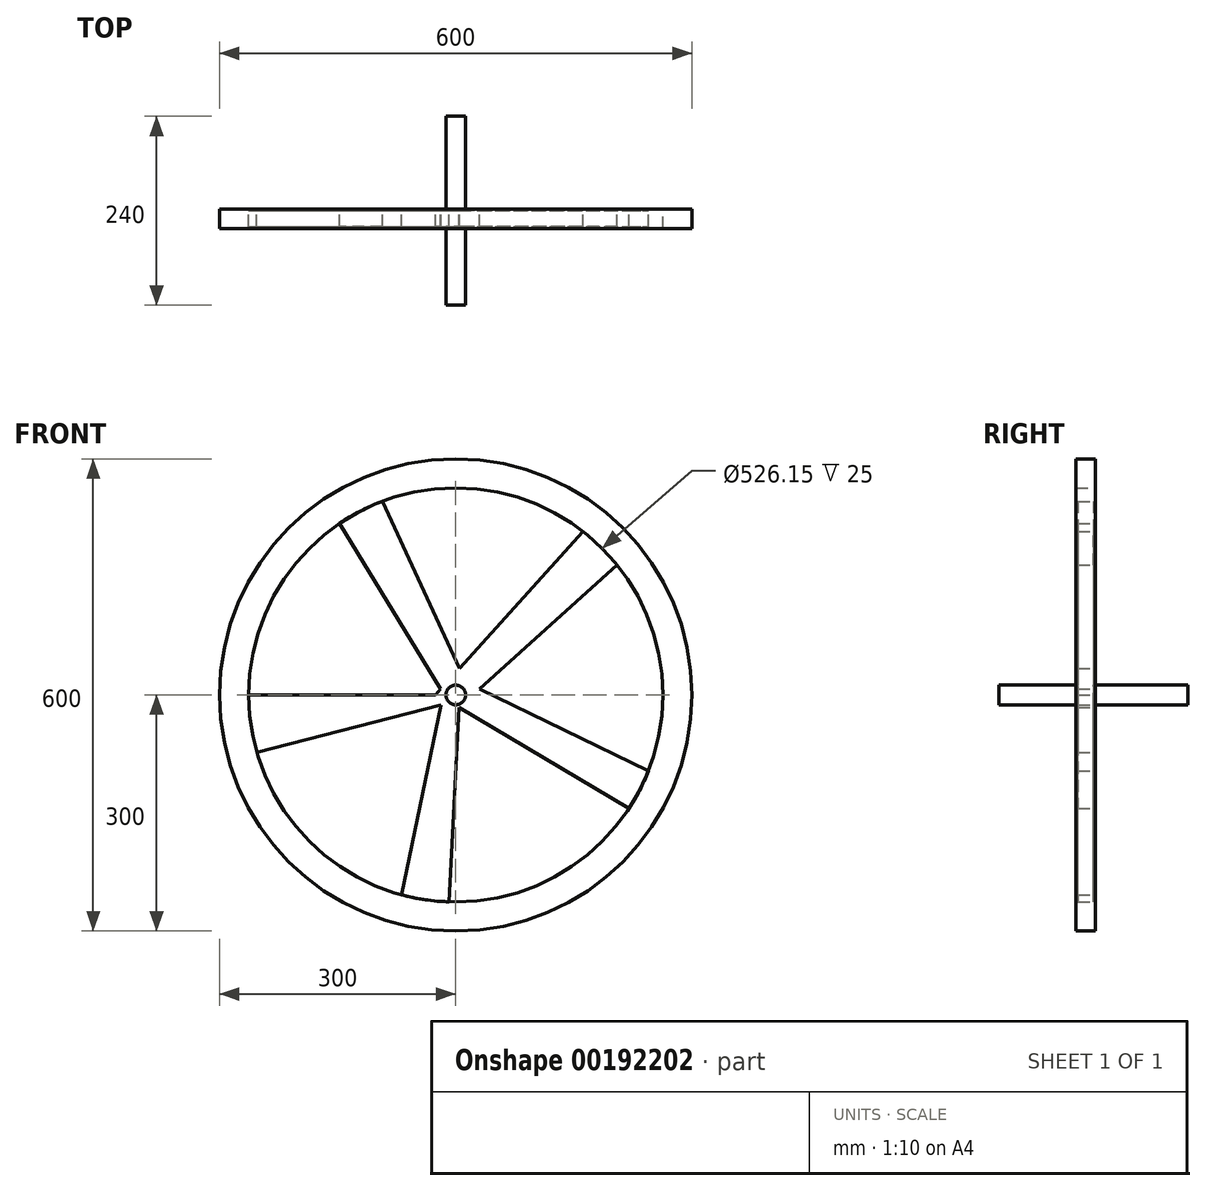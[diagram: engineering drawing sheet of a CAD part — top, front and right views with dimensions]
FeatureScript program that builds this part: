
annotation { "Feature Type Name" : "Feature", "Feature Type Description" : "" }
export const myFeature = defineFeature(function(context is Context, id is Id, definition is map)
    precondition{}
    {
        {
            var Q0;
            Q0=qCreatedBy(makeId("Front.planeOp"),FACE);
            var sketch = newSketch(context, id + "F0", { "sketchPlane" : qUnion([Q0])});
            skCircle(sketch, "E0", {"center": v(0, 0) * mm, "radius": 300 * mm});
            skCircle(sketch, "E1", {"center": v(0, 0) * mm, "radius": 263.08 * mm});
            skLineSegment(sketch, "E2.0", {"start": v(-42.18, -280.34) * mm, "end": v(-69.08, -253.84) * mm});
            skLineSegment(sketch, "E2.2", {"start": v(-130.66, 251.59) * mm, "end": v(-93.32, 245.97) * mm});
            skLineSegment(sketch, "E2.3", {"start": v(198.9, 202) * mm, "end": v(205.1, 164.76) * mm});
            skLineSegment(sketch, "E2.4", {"start": v(253.58, -126.74) * mm, "end": v(220.07, -144.14) * mm});
            skPoint(sketch, "E2.0.midPoint", {"position": v(-160.91, -163.43) * mm});
            skLineSegment(sketch, "E3", {"start": v(-147.54, 217.81) * mm, "end": v(-19.08, 7.43) * mm});
            skLineSegment(sketch, "E4", {"start": v(-93.32, 245.97) * mm, "end": v(12.84, 15.73) * mm});
            skLineSegment(sketch, "E5", {"start": v(12.84, 15.73) * mm, "end": v(244.63, -96.78) * mm});
            skLineSegment(sketch, "E6", {"start": v(-9.72, -7.9) * mm, "end": v(-6.77, -9.64) * mm});
            skLineSegment(sketch, "E7", {"start": v(161.56, 207.63) * mm, "end": v(4.58, 33.65) * mm});
            skLineSegment(sketch, "E8", {"start": v(205.1, 164.76) * mm, "end": v(30.14, 7.33) * mm});
            skLineSegment(sketch, "E9", {"start": v(-263.08, 0) * mm, "end": v(-25.78, 0) * mm});
            skLineSegment(sketch, "E10", {"start": v(-252.74, -73.01) * mm, "end": v(-18.49, -12.66) * mm});
            skLineSegment(sketch, "E11", {"start": v(-8.66, -262.93) * mm, "end": v(4.11, -16.1) * mm});
            skLineSegment(sketch, "E12.trimOffspring", {"start": v(-19.08, 7.43) * mm, "end": v(-25.78, 0) * mm});
            skLineSegment(sketch, "E13", {"start": v(-69.08, -253.84) * mm, "end": v(-18.49, -12.66) * mm});
            skLineSegment(sketch, "E14.trimOffspring", {"start": v(4.11, -16.1) * mm, "end": v(220.07, -144.14) * mm});
            skPoint(sketch, "E15.end.orphan", {"position": v(12.84, 5.87) * mm});
            skPoint(sketch, "E16.trimOffspring.end.orphan", {"position": v(0, -7.9) * mm});
            skLineSegment(sketch, "E17.trimOffspring", {"start": v(-147.54, 217.81) * mm, "end": v(-130.66, 251.59) * mm});
            skPoint(sketch, "E18.orphan", {"position": v(-279.65, -46.52) * mm});
            skLineSegment(sketch, "E19.trimOffspring", {"start": v(247.39, -89.5) * mm, "end": v(253.58, -126.74) * mm});
            skLineSegment(sketch, "E20.trimOffspring", {"start": v(-8.66, -262.93) * mm, "end": v(-42.18, -280.34) * mm});
            skLineSegment(sketch, "E21", {"start": v(161.56, 207.63) * mm, "end": v(198.9, 202) * mm});
            skLineSegment(sketch, "E22", {"start": v(-252.74, -73.01) * mm, "end": v(-279.65, -46.52) * mm});
            skLineSegment(sketch, "E23", {"start": v(-279.65, -46.52) * mm, "end": v(-263.08, 0) * mm});
            skSolve(sketch);
        }
        {
            var Q0;
            Q0=makeQuery(id+"F0.imprint","IMPRINT",FACE,{"disambiguationData":[TD([[makeQuery(id+"F0.imprint","IMPRINT",EDGE,{"derivedFrom":sQuery(id+"F0.wireOp",EDGE,"E0")}),1.0]])]});
            var Q1;
            {var subQ0=sQuery(id+"F0.wireOp",EDGE,"E2.2");Q1=makeQuery(id+"F0.imprint","IMPRINT",FACE,{"disambiguationData":[TD([[makeQuery(id+"F0.imprint","IMPRINT",EDGE,{"derivedFrom":subQ0}),-1.0]])]});}
            var Q2;
            {var subQ2=sQuery(id+"F0.wireOp",EDGE,"E22");Q2=makeQuery(id+"F0.imprint","IMPRINT",FACE,{"disambiguationData":[TD([[makeQuery(id+"F0.imprint","IMPRINT",EDGE,{"derivedFrom":subQ2}),-1.0]])]});}
            var Q3;
            {var subQ0=sQuery(id+"F0.wireOp",EDGE,"E2.0");Q3=makeQuery(id+"F0.imprint","IMPRINT",FACE,{"disambiguationData":[TD([[makeQuery(id+"F0.imprint","IMPRINT",EDGE,{"derivedFrom":subQ0}),-1.0]])]});}
            var Q4;
            {var subQ0=sQuery(id+"F0.wireOp",EDGE,"E2.4");Q4=makeQuery(id+"F0.imprint","IMPRINT",FACE,{"disambiguationData":[TD([[makeQuery(id+"F0.imprint","IMPRINT",EDGE,{"derivedFrom":subQ0}),-1.0]])]});}
            var Q5;
            {var subQ0=sQuery(id+"F0.wireOp",EDGE,"E2.3");Q5=makeQuery(id+"F0.imprint","IMPRINT",FACE,{"disambiguationData":[TD([[makeQuery(id+"F0.imprint","IMPRINT",EDGE,{"derivedFrom":subQ0}),-1.0]])]});}
            extrude(context, id + "F1", {"entities" : qUnion([Q0, Q1, Q2, Q3, Q4, Q5]), "depth" : 25 * mm, "symmetric" : true});
        }
        {
            var Q0;
            {var subQ7=sQuery(id+"F0.wireOp",EDGE,"E3");Q0=makeQuery(id+"F0.imprint","IMPRINT",FACE,{"disambiguationData":[TD([[makeQuery(id+"F0.imprint","IMPRINT",EDGE,{"derivedFrom":subQ7}),1.0]])]});}
            var Q1;
            {var subQ0=sQuery(id+"F0.wireOp",EDGE,"E7");Q1=makeQuery(id+"F0.imprint","IMPRINT",FACE,{"disambiguationData":[TD([[makeQuery(id+"F0.imprint","IMPRINT",EDGE,{"derivedFrom":subQ0}),1.0]])]});}
            extrude(context, id + "F2", {"entities" : qUnion([Q0, Q1]), "operationType" : NewBodyOperationType.ADD, "depth" : 20 * mm, "symmetric" : true});
        }
        {
            var Q0;
            Q0=makeQuery(id+"F2.opExtrude","CAP_FACE",FACE,{"disambiguationData":[OSD([sQuery(id+"F0.wireOp",EDGE,"E1"),sQuery(id+"F0.wireOp",EDGE,"E3"),sQuery(id+"F0.wireOp",EDGE,"E4"),sQuery(id+"F0.wireOp",EDGE,"E5"),sQuery(id+"F0.wireOp",EDGE,"E7"),sQuery(id+"F0.wireOp",EDGE,"E8"),sQuery(id+"F0.wireOp",EDGE,"E9"),sQuery(id+"F0.wireOp",EDGE,"E10"),sQuery(id+"F0.wireOp",EDGE,"E11"),sQuery(id+"F0.wireOp",EDGE,"E12.trimOffspring"),sQuery(id+"F0.wireOp",EDGE,"E13"),sQuery(id+"F0.wireOp",EDGE,"E14.trimOffspring")])],"isStart":true});
            var sketch = newSketch(context, id + "F3", { "sketchPlane" : qUnion([Q0])});
            skCircle(sketch, "E24", {"center": v(0, 0) * mm, "radius": 12.5 * mm});
            skSolve(sketch);
        }
        {
            var Q0;
            Q0 = qSketchRegion(id + "F3", true);
            extrude(context, id + "F4", {"entities" : qUnion([Q0]), "operationType" : NewBodyOperationType.ADD, "depth" : 240 * mm, "symmetric" : true});
        }
    });
